# Revit family: Indoor_Pendant Lamp_Santa&Cole_HeadHat Bowl
name_source: partatom
category: Luminarias
revit_build: Autodesk Revit 2018 (Build: 20190510_1515(x64)
units: mm (PartAtom-declared; Revit-internal decimal feet)

## family parameters
Anfitrión = Cara
Compartido = No
Corte con vacíos al cargar = No
Cota de conector redondo = Diámetro de uso
Origen de luz = Sí
Punto de cálculo de habitación = No
Tipo de pieza = Normal

## types (4) — shared parameters
Archivo de red fotométrica = HATS02_500mA.IES
Assembly Instructions - CE = https://www.santacole.com
Assembly Instructions - UL = https://www.santacole.com
Cambio de temperatura de color de luz atenuada = <Ninguno>
Carga aparente = 8 W
Elevación por defecto = 1219 mm
Energy Label = https://www.santacole.com
Fabricante = Santa & Cole
Filtro de color = 16777215
Load = 10 W
Manufacturer website = http://www.santacole.com
Modelo = HeadHat Bowl
Technical Information = https://www.santacole.com
URL = https://www.santacole.com
Voltaje (90-305 V) = 220 V
Ángulo de inclinación = -90.00°

## per-type parameters (varying)
| type | Code | Lampshade Material | Visibility_L | Visibility_S |
| HeadHat Bowl S - White | HEFxx+HEL0x+HATS1x | Santa & Cole - White Ceramic | No | Sí |
| HeadHat Bowl L - Black | HEFxx+HEL0x+HATL1x | Santa & Cole - Black Ceramic | Sí | No |
| HeadHat Bowl S - Black | HEFxx+HEL0x+HATS1x | Santa & Cole - Black Ceramic | No | Sí |
| HeadHat Bowl L - White | HEFxx+HEL0x+HATL1x | Santa & Cole - White Ceramic | Sí | No |

## geometry (parser evidence)
native form markers: Blend x4, Sweep x6
no freeform markers — native parametric forms only
